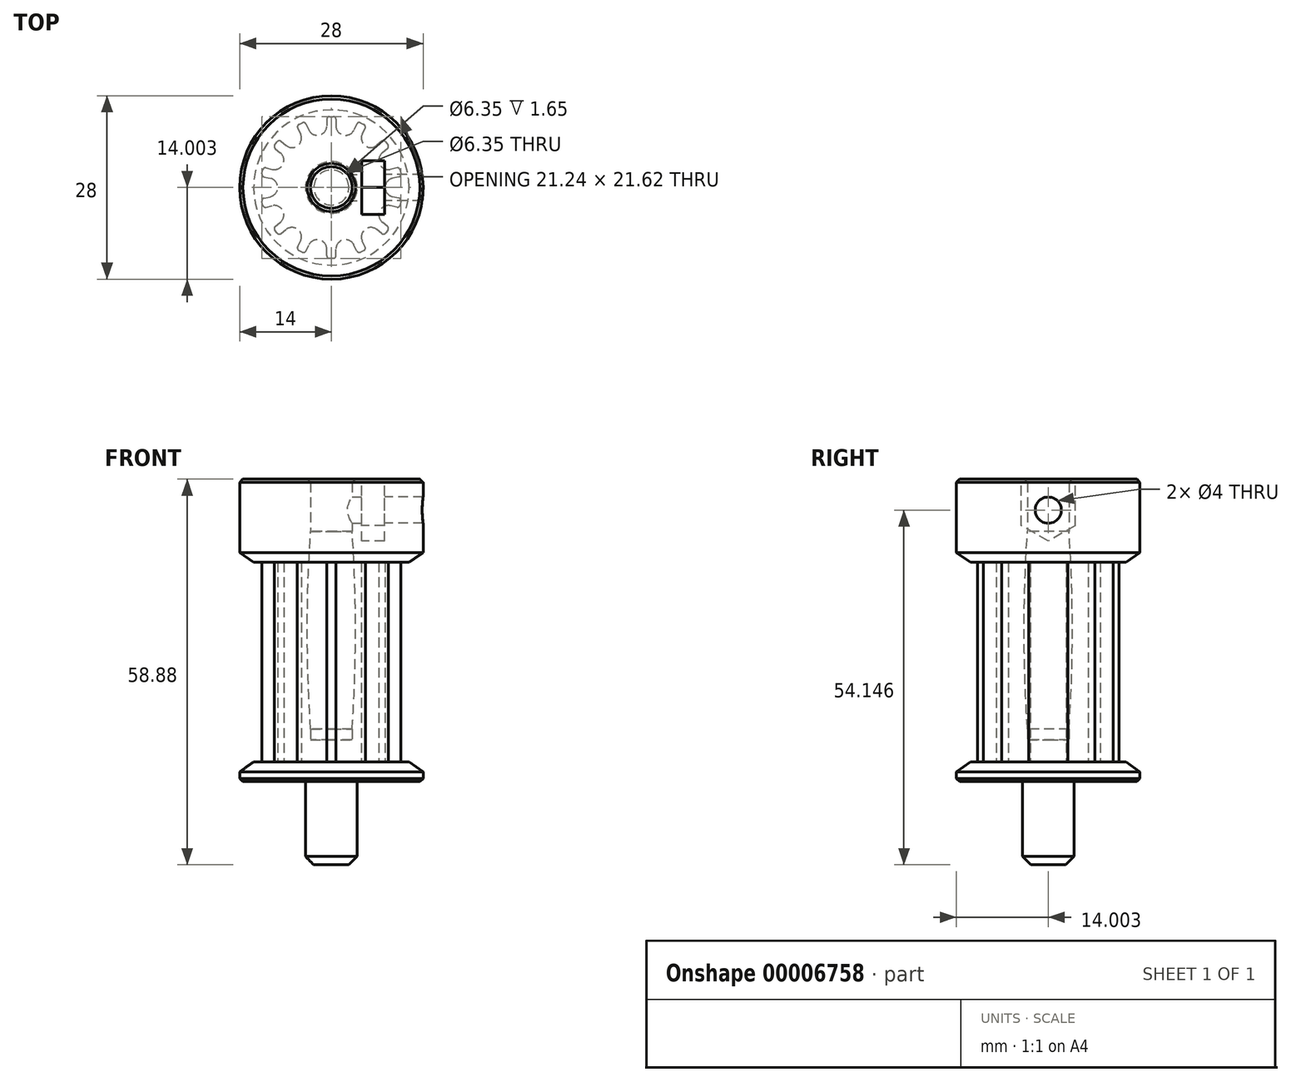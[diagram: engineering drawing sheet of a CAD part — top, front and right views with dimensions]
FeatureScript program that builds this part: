
annotation { "Feature Type Name" : "Feature", "Feature Type Description" : "" }
export const myFeature = defineFeature(function(context is Context, id is Id, definition is map)
    precondition{}
    {
        {
            var Q0;
            Q0=qCreatedBy(makeId("Top.planeOp"),FACE);
            var sketch = newSketch(context, id + "F0", { "sketchPlane" : qUnion([Q0])});
            skLineSegment(sketch, "E0", {"start": v(-0.3, 10.12) * mm, "end": v(0.3, 10.12) * mm});
            skPoint(sketch, "E1", {"position": v(0, 10.12) * mm});
            skArc(sketch, "E2", {"start": v(0.3, 10.12) * mm, "mid": v(0.58, 10) * mm, "end": v(0.7, 9.72) * mm});
            skArc(sketch, "E3", {"start": v(-0.3, 10.12) * mm, "mid": v(-0.58, 10) * mm, "end": v(-0.7, 9.72) * mm});
            skLineSegment(sketch, "E4", {"start": v(-0.7, 9.72) * mm, "end": v(-0.7, 8.72) * mm});
            skLineSegment(sketch, "E5", {"start": v(0.7, 9.72) * mm, "end": v(0.7, 8.72) * mm});
            skArc(sketch, "E6", {"start": v(-0.7, 8.72) * mm, "mid": v(-1.83, 7.3) * mm, "end": v(-3.45, 8.09) * mm});
            skArc(sketch, "E7.1.0", {"start": v(-4.71, 7.48) * mm, "mid": v(-5.12, 5.72) * mm, "end": v(-6.92, 5.72) * mm});
            skLineSegment(sketch, "E7.1.1", {"start": v(-5.15, 8.38) * mm, "end": v(-4.71, 7.48) * mm});
            skArc(sketch, "E7.1.2", {"start": v(-4.96, 8.91) * mm, "mid": v(-5.17, 8.69) * mm, "end": v(-5.15, 8.38) * mm});
            skLineSegment(sketch, "E7.1.3", {"start": v(-4.96, 8.91) * mm, "end": v(-4.42, 9.17) * mm});
            skArc(sketch, "E7.1.4", {"start": v(-4.42, 9.17) * mm, "mid": v(-4.12, 9.2) * mm, "end": v(-3.89, 8.99) * mm});
            skLineSegment(sketch, "E7.1.5", {"start": v(-3.89, 8.99) * mm, "end": v(-3.45, 8.09) * mm});
            skArc(sketch, "E7.2.0", {"start": v(-7.8, 4.62) * mm, "mid": v(-7.4, 2.86) * mm, "end": v(-9.02, 2.08) * mm});
            skLineSegment(sketch, "E7.2.1", {"start": v(-8.58, 5.25) * mm, "end": v(-7.8, 4.62) * mm});
            skArc(sketch, "E7.2.2", {"start": v(-8.64, 5.8) * mm, "mid": v(-8.73, 5.52) * mm, "end": v(-8.58, 5.25) * mm});
            skLineSegment(sketch, "E7.2.3", {"start": v(-8.64, 5.8) * mm, "end": v(-8.27, 6.28) * mm});
            skArc(sketch, "E7.2.4", {"start": v(-8.27, 6.28) * mm, "mid": v(-8, 6.43) * mm, "end": v(-7.7, 6.34) * mm});
            skLineSegment(sketch, "E7.2.5", {"start": v(-7.7, 6.34) * mm, "end": v(-6.92, 5.72) * mm});
            skPoint(sketch, "E7.center", {"position": v(0, -0.7) * mm});
            skArc(sketch, "E8.3.3.0", {"start": v(-9.33, 0.72) * mm, "mid": v(-8.2, -0.7) * mm, "end": v(-9.33, -2.1) * mm});
            skLineSegment(sketch, "E8.4.3.0", {"start": v(-10.3, 0.94) * mm, "end": v(-9.33, 0.72) * mm});
            skArc(sketch, "E8.7.3.0", {"start": v(-10.6, 1.42) * mm, "mid": v(-10.56, 1.11) * mm, "end": v(-10.3, 0.94) * mm});
            skLineSegment(sketch, "E8.11.3.0", {"start": v(-10.6, 1.42) * mm, "end": v(-10.47, 2) * mm});
            skArc(sketch, "E8.14.3.0", {"start": v(-10.47, 2) * mm, "mid": v(-10.3, 2.25) * mm, "end": v(-10, 2.3) * mm});
            skLineSegment(sketch, "E8.18.3.0", {"start": v(-10, 2.3) * mm, "end": v(-9.02, 2.08) * mm});
            skArc(sketch, "E8.3.4.0", {"start": v(-9.02, -3.47) * mm, "mid": v(-7.4, -4.26) * mm, "end": v(-7.8, -6.02) * mm});
            skLineSegment(sketch, "E8.4.4.0", {"start": v(-10, -3.7) * mm, "end": v(-9.02, -3.47) * mm});
            skArc(sketch, "E8.7.4.0", {"start": v(-10.47, -3.4) * mm, "mid": v(-10.3, -3.64) * mm, "end": v(-10, -3.7) * mm});
            skLineSegment(sketch, "E8.11.4.0", {"start": v(-10.47, -3.4) * mm, "end": v(-10.6, -2.81) * mm});
            skArc(sketch, "E8.14.4.0", {"start": v(-10.6, -2.81) * mm, "mid": v(-10.56, -2.5) * mm, "end": v(-10.3, -2.33) * mm});
            skLineSegment(sketch, "E8.18.4.0", {"start": v(-10.3, -2.33) * mm, "end": v(-9.33, -2.1) * mm});
            skArc(sketch, "E8.3.5.0", {"start": v(-6.92, -7.11) * mm, "mid": v(-5.12, -7.11) * mm, "end": v(-4.71, -8.87) * mm});
            skLineSegment(sketch, "E8.4.5.0", {"start": v(-7.7, -7.74) * mm, "end": v(-6.92, -7.11) * mm});
            skArc(sketch, "E8.7.5.0", {"start": v(-8.27, -7.67) * mm, "mid": v(-8, -7.82) * mm, "end": v(-7.7, -7.74) * mm});
            skLineSegment(sketch, "E8.11.5.0", {"start": v(-8.27, -7.67) * mm, "end": v(-8.64, -7.2) * mm});
            skArc(sketch, "E8.14.5.0", {"start": v(-8.64, -7.2) * mm, "mid": v(-8.73, -6.9) * mm, "end": v(-8.58, -6.64) * mm});
            skLineSegment(sketch, "E8.18.5.0", {"start": v(-8.58, -6.64) * mm, "end": v(-7.8, -6.02) * mm});
            skArc(sketch, "E8.3.6.0", {"start": v(-3.45, -9.48) * mm, "mid": v(-1.83, -8.7) * mm, "end": v(-0.7, -10.1) * mm});
            skLineSegment(sketch, "E8.4.6.0", {"start": v(-3.89, -10.38) * mm, "end": v(-3.45, -9.48) * mm});
            skArc(sketch, "E8.7.6.0", {"start": v(-4.42, -10.57) * mm, "mid": v(-4.12, -10.59) * mm, "end": v(-3.89, -10.38) * mm});
            skLineSegment(sketch, "E8.11.6.0", {"start": v(-4.42, -10.57) * mm, "end": v(-4.96, -10.3) * mm});
            skArc(sketch, "E8.14.6.0", {"start": v(-4.96, -10.3) * mm, "mid": v(-5.17, -10.08) * mm, "end": v(-5.15, -9.77) * mm});
            skLineSegment(sketch, "E8.18.6.0", {"start": v(-5.15, -9.77) * mm, "end": v(-4.71, -8.87) * mm});
            skArc(sketch, "E8.3.7.0", {"start": v(0.7, -10.1) * mm, "mid": v(1.83, -8.7) * mm, "end": v(3.45, -9.48) * mm});
            skLineSegment(sketch, "E8.4.7.0", {"start": v(0.7, -11.1) * mm, "end": v(0.7, -10.1) * mm});
            skArc(sketch, "E8.7.7.0", {"start": v(0.3, -11.5) * mm, "mid": v(0.58, -11.4) * mm, "end": v(0.7, -11.1) * mm});
            skLineSegment(sketch, "E8.11.7.0", {"start": v(0.3, -11.5) * mm, "end": v(-0.3, -11.5) * mm});
            skArc(sketch, "E8.14.7.0", {"start": v(-0.3, -11.5) * mm, "mid": v(-0.58, -11.4) * mm, "end": v(-0.7, -11.1) * mm});
            skLineSegment(sketch, "E8.18.7.0", {"start": v(-0.7, -11.1) * mm, "end": v(-0.7, -10.1) * mm});
            skArc(sketch, "E8.3.8.0", {"start": v(4.71, -8.87) * mm, "mid": v(5.12, -7.11) * mm, "end": v(6.92, -7.11) * mm});
            skLineSegment(sketch, "E8.4.8.0", {"start": v(5.15, -9.77) * mm, "end": v(4.71, -8.87) * mm});
            skArc(sketch, "E8.7.8.0", {"start": v(4.96, -10.3) * mm, "mid": v(5.17, -10.08) * mm, "end": v(5.15, -9.77) * mm});
            skLineSegment(sketch, "E8.11.8.0", {"start": v(4.96, -10.3) * mm, "end": v(4.42, -10.57) * mm});
            skArc(sketch, "E8.14.8.0", {"start": v(4.42, -10.57) * mm, "mid": v(4.12, -10.59) * mm, "end": v(3.89, -10.38) * mm});
            skLineSegment(sketch, "E8.18.8.0", {"start": v(3.89, -10.38) * mm, "end": v(3.45, -9.48) * mm});
            skArc(sketch, "E8.3.9.0", {"start": v(7.8, -6.02) * mm, "mid": v(7.4, -4.26) * mm, "end": v(9.02, -3.47) * mm});
            skLineSegment(sketch, "E8.4.9.0", {"start": v(8.58, -6.64) * mm, "end": v(7.8, -6.02) * mm});
            skArc(sketch, "E8.7.9.0", {"start": v(8.64, -7.2) * mm, "mid": v(8.73, -6.9) * mm, "end": v(8.58, -6.64) * mm});
            skLineSegment(sketch, "E8.11.9.0", {"start": v(8.64, -7.2) * mm, "end": v(8.27, -7.67) * mm});
            skArc(sketch, "E8.14.9.0", {"start": v(8.27, -7.67) * mm, "mid": v(8, -7.82) * mm, "end": v(7.7, -7.74) * mm});
            skLineSegment(sketch, "E8.18.9.0", {"start": v(7.7, -7.74) * mm, "end": v(6.92, -7.11) * mm});
            skArc(sketch, "E8.3.10.0", {"start": v(9.33, -2.1) * mm, "mid": v(8.2, -0.7) * mm, "end": v(9.33, 0.72) * mm});
            skLineSegment(sketch, "E8.4.10.0", {"start": v(10.3, -2.33) * mm, "end": v(9.33, -2.1) * mm});
            skArc(sketch, "E8.7.10.0", {"start": v(10.6, -2.81) * mm, "mid": v(10.56, -2.5) * mm, "end": v(10.3, -2.33) * mm});
            skLineSegment(sketch, "E8.11.10.0", {"start": v(10.6, -2.81) * mm, "end": v(10.47, -3.4) * mm});
            skArc(sketch, "E8.14.10.0", {"start": v(10.47, -3.4) * mm, "mid": v(10.3, -3.64) * mm, "end": v(10, -3.7) * mm});
            skLineSegment(sketch, "E8.18.10.0", {"start": v(10, -3.7) * mm, "end": v(9.02, -3.47) * mm});
            skArc(sketch, "E8.3.11.0", {"start": v(9.02, 2.08) * mm, "mid": v(7.4, 2.86) * mm, "end": v(7.8, 4.62) * mm});
            skLineSegment(sketch, "E8.4.11.0", {"start": v(10, 2.3) * mm, "end": v(9.02, 2.08) * mm});
            skArc(sketch, "E8.7.11.0", {"start": v(10.47, 2) * mm, "mid": v(10.3, 2.25) * mm, "end": v(10, 2.3) * mm});
            skLineSegment(sketch, "E8.11.11.0", {"start": v(10.47, 2) * mm, "end": v(10.6, 1.42) * mm});
            skArc(sketch, "E8.14.11.0", {"start": v(10.6, 1.42) * mm, "mid": v(10.56, 1.11) * mm, "end": v(10.3, 0.94) * mm});
            skLineSegment(sketch, "E8.18.11.0", {"start": v(10.3, 0.94) * mm, "end": v(9.33, 0.72) * mm});
            skArc(sketch, "E8.3.12.0", {"start": v(6.92, 5.72) * mm, "mid": v(5.12, 5.72) * mm, "end": v(4.71, 7.48) * mm});
            skLineSegment(sketch, "E8.4.12.0", {"start": v(7.7, 6.34) * mm, "end": v(6.92, 5.72) * mm});
            skArc(sketch, "E8.7.12.0", {"start": v(8.27, 6.28) * mm, "mid": v(8, 6.43) * mm, "end": v(7.7, 6.34) * mm});
            skLineSegment(sketch, "E8.11.12.0", {"start": v(8.27, 6.28) * mm, "end": v(8.64, 5.8) * mm});
            skArc(sketch, "E8.14.12.0", {"start": v(8.64, 5.8) * mm, "mid": v(8.73, 5.52) * mm, "end": v(8.58, 5.25) * mm});
            skLineSegment(sketch, "E8.18.12.0", {"start": v(8.58, 5.25) * mm, "end": v(7.8, 4.62) * mm});
            skArc(sketch, "E8.3.13.0", {"start": v(3.45, 8.09) * mm, "mid": v(1.83, 7.3) * mm, "end": v(0.7, 8.72) * mm});
            skLineSegment(sketch, "E8.4.13.0", {"start": v(3.89, 8.99) * mm, "end": v(3.45, 8.09) * mm});
            skArc(sketch, "E8.7.13.0", {"start": v(4.42, 9.17) * mm, "mid": v(4.12, 9.2) * mm, "end": v(3.89, 8.99) * mm});
            skLineSegment(sketch, "E8.11.13.0", {"start": v(4.42, 9.17) * mm, "end": v(4.96, 8.91) * mm});
            skArc(sketch, "E8.14.13.0", {"start": v(4.96, 8.91) * mm, "mid": v(5.17, 8.69) * mm, "end": v(5.15, 8.38) * mm});
            skLineSegment(sketch, "E8.18.13.0", {"start": v(5.15, 8.38) * mm, "end": v(4.71, 7.48) * mm});
            skCircle(sketch, "E9", {"center": v(0, -0.7) * mm, "radius": 10.81 * mm, "construction": true});
            skCircle(sketch, "E10", {"center": v(0, -0.7) * mm, "radius": 3.18 * mm});
            skSolve(sketch);
        }
        {
            var Q0;
            Q0=makeQuery(id+"F0.imprint","IMPRINT",FACE,{"disambiguationData":[TD([[makeQuery(id+"F0.imprint","IMPRINT",EDGE,{"derivedFrom":sQuery(id+"F0.wireOp",EDGE,"E0")}),-1.0]])]});
            extrude(context, id + "F1", {"entities" : qUnion([Q0]), "endBound" : BoundingType.SYMMETRIC, "depth" : 30.48 * mm, "offsetDistance" : 25 * mm});
        }
        {
            var Q0;
            Q0=makeQuery(id+"F1.opExtrude","CAP_FACE",FACE,{"disambiguationData":[OSD([sQuery(id+"F0.wireOp",EDGE,"E0"),sQuery(id+"F0.wireOp",EDGE,"E2"),sQuery(id+"F0.wireOp",EDGE,"E3"),sQuery(id+"F0.wireOp",EDGE,"E4"),sQuery(id+"F0.wireOp",EDGE,"E5"),sQuery(id+"F0.wireOp",EDGE,"E6"),sQuery(id+"F0.wireOp",EDGE,"E7.1.0"),sQuery(id+"F0.wireOp",EDGE,"E7.1.1"),sQuery(id+"F0.wireOp",EDGE,"E7.1.2"),sQuery(id+"F0.wireOp",EDGE,"E7.1.3"),sQuery(id+"F0.wireOp",EDGE,"E7.1.4"),sQuery(id+"F0.wireOp",EDGE,"E7.1.5"),sQuery(id+"F0.wireOp",EDGE,"E7.2.0"),sQuery(id+"F0.wireOp",EDGE,"E7.2.1"),sQuery(id+"F0.wireOp",EDGE,"E7.2.2"),sQuery(id+"F0.wireOp",EDGE,"E7.2.3"),sQuery(id+"F0.wireOp",EDGE,"E7.2.4"),sQuery(id+"F0.wireOp",EDGE,"E7.2.5"),sQuery(id+"F0.wireOp",EDGE,"E8.3.3.0"),sQuery(id+"F0.wireOp",EDGE,"E8.4.3.0"),sQuery(id+"F0.wireOp",EDGE,"E8.7.3.0"),sQuery(id+"F0.wireOp",EDGE,"E8.11.3.0"),sQuery(id+"F0.wireOp",EDGE,"E8.14.3.0"),sQuery(id+"F0.wireOp",EDGE,"E8.18.3.0"),sQuery(id+"F0.wireOp",EDGE,"E8.3.4.0"),sQuery(id+"F0.wireOp",EDGE,"E8.4.4.0"),sQuery(id+"F0.wireOp",EDGE,"E8.7.4.0"),sQuery(id+"F0.wireOp",EDGE,"E8.11.4.0"),sQuery(id+"F0.wireOp",EDGE,"E8.14.4.0"),sQuery(id+"F0.wireOp",EDGE,"E8.18.4.0"),sQuery(id+"F0.wireOp",EDGE,"E8.3.5.0"),sQuery(id+"F0.wireOp",EDGE,"E8.4.5.0"),sQuery(id+"F0.wireOp",EDGE,"E8.7.5.0"),sQuery(id+"F0.wireOp",EDGE,"E8.11.5.0"),sQuery(id+"F0.wireOp",EDGE,"E8.14.5.0"),sQuery(id+"F0.wireOp",EDGE,"E8.18.5.0"),sQuery(id+"F0.wireOp",EDGE,"E8.3.6.0"),sQuery(id+"F0.wireOp",EDGE,"E8.4.6.0"),sQuery(id+"F0.wireOp",EDGE,"E8.7.6.0"),sQuery(id+"F0.wireOp",EDGE,"E8.11.6.0"),sQuery(id+"F0.wireOp",EDGE,"E8.14.6.0"),sQuery(id+"F0.wireOp",EDGE,"E8.18.6.0"),sQuery(id+"F0.wireOp",EDGE,"E8.3.7.0"),sQuery(id+"F0.wireOp",EDGE,"E8.4.7.0"),sQuery(id+"F0.wireOp",EDGE,"E8.7.7.0"),sQuery(id+"F0.wireOp",EDGE,"E8.11.7.0"),sQuery(id+"F0.wireOp",EDGE,"E8.14.7.0"),sQuery(id+"F0.wireOp",EDGE,"E8.18.7.0"),sQuery(id+"F0.wireOp",EDGE,"E8.3.8.0"),sQuery(id+"F0.wireOp",EDGE,"E8.4.8.0"),sQuery(id+"F0.wireOp",EDGE,"E8.7.8.0"),sQuery(id+"F0.wireOp",EDGE,"E8.11.8.0"),sQuery(id+"F0.wireOp",EDGE,"E8.14.8.0"),sQuery(id+"F0.wireOp",EDGE,"E8.18.8.0"),sQuery(id+"F0.wireOp",EDGE,"E8.3.9.0"),sQuery(id+"F0.wireOp",EDGE,"E8.4.9.0"),sQuery(id+"F0.wireOp",EDGE,"E8.7.9.0"),sQuery(id+"F0.wireOp",EDGE,"E8.11.9.0"),sQuery(id+"F0.wireOp",EDGE,"E8.14.9.0"),sQuery(id+"F0.wireOp",EDGE,"E8.18.9.0"),sQuery(id+"F0.wireOp",EDGE,"E8.3.10.0"),sQuery(id+"F0.wireOp",EDGE,"E8.4.10.0"),sQuery(id+"F0.wireOp",EDGE,"E8.7.10.0"),sQuery(id+"F0.wireOp",EDGE,"E8.11.10.0"),sQuery(id+"F0.wireOp",EDGE,"E8.14.10.0"),sQuery(id+"F0.wireOp",EDGE,"E8.18.10.0"),sQuery(id+"F0.wireOp",EDGE,"E8.3.11.0"),sQuery(id+"F0.wireOp",EDGE,"E8.4.11.0"),sQuery(id+"F0.wireOp",EDGE,"E8.7.11.0"),sQuery(id+"F0.wireOp",EDGE,"E8.11.11.0"),sQuery(id+"F0.wireOp",EDGE,"E8.14.11.0"),sQuery(id+"F0.wireOp",EDGE,"E8.18.11.0"),sQuery(id+"F0.wireOp",EDGE,"E8.3.12.0"),sQuery(id+"F0.wireOp",EDGE,"E8.4.12.0"),sQuery(id+"F0.wireOp",EDGE,"E8.7.12.0"),sQuery(id+"F0.wireOp",EDGE,"E8.11.12.0"),sQuery(id+"F0.wireOp",EDGE,"E8.14.12.0"),sQuery(id+"F0.wireOp",EDGE,"E8.18.12.0"),sQuery(id+"F0.wireOp",EDGE,"E8.3.13.0"),sQuery(id+"F0.wireOp",EDGE,"E8.4.13.0"),sQuery(id+"F0.wireOp",EDGE,"E8.7.13.0"),sQuery(id+"F0.wireOp",EDGE,"E8.11.13.0"),sQuery(id+"F0.wireOp",EDGE,"E8.14.13.0"),sQuery(id+"F0.wireOp",EDGE,"E8.18.13.0"),sQuery(id+"F0.wireOp",EDGE,"c70ca20e-aa8e-449a-a5f3-8252f9445d40.3.14.0"),sQuery(id+"F0.wireOp",EDGE,"c70ca20e-aa8e-449a-a5f3-8252f9445d40.4.14.0"),sQuery(id+"F0.wireOp",EDGE,"c70ca20e-aa8e-449a-a5f3-8252f9445d40.7.14.0"),sQuery(id+"F0.wireOp",EDGE,"c70ca20e-aa8e-449a-a5f3-8252f9445d40.11.14.0"),sQuery(id+"F0.wireOp",EDGE,"c70ca20e-aa8e-449a-a5f3-8252f9445d40.14.14.0"),sQuery(id+"F0.wireOp",EDGE,"c70ca20e-aa8e-449a-a5f3-8252f9445d40.18.14.0"),sQuery(id+"F0.wireOp",EDGE,"c70ca20e-aa8e-449a-a5f3-8252f9445d40.3.15.0"),sQuery(id+"F0.wireOp",EDGE,"c70ca20e-aa8e-449a-a5f3-8252f9445d40.4.15.0"),sQuery(id+"F0.wireOp",EDGE,"c70ca20e-aa8e-449a-a5f3-8252f9445d40.7.15.0"),sQuery(id+"F0.wireOp",EDGE,"c70ca20e-aa8e-449a-a5f3-8252f9445d40.11.15.0"),sQuery(id+"F0.wireOp",EDGE,"c70ca20e-aa8e-449a-a5f3-8252f9445d40.14.15.0"),sQuery(id+"F0.wireOp",EDGE,"c70ca20e-aa8e-449a-a5f3-8252f9445d40.18.15.0"),sQuery(id+"F0.wireOp",EDGE,"c70ca20e-aa8e-449a-a5f3-8252f9445d40.3.16.0"),sQuery(id+"F0.wireOp",EDGE,"c70ca20e-aa8e-449a-a5f3-8252f9445d40.4.16.0"),sQuery(id+"F0.wireOp",EDGE,"c70ca20e-aa8e-449a-a5f3-8252f9445d40.7.16.0"),sQuery(id+"F0.wireOp",EDGE,"c70ca20e-aa8e-449a-a5f3-8252f9445d40.11.16.0"),sQuery(id+"F0.wireOp",EDGE,"c70ca20e-aa8e-449a-a5f3-8252f9445d40.14.16.0"),sQuery(id+"F0.wireOp",EDGE,"c70ca20e-aa8e-449a-a5f3-8252f9445d40.18.16.0"),sQuery(id+"F0.wireOp",EDGE,"c70ca20e-aa8e-449a-a5f3-8252f9445d40.3.17.0"),sQuery(id+"F0.wireOp",EDGE,"c70ca20e-aa8e-449a-a5f3-8252f9445d40.4.17.0"),sQuery(id+"F0.wireOp",EDGE,"c70ca20e-aa8e-449a-a5f3-8252f9445d40.7.17.0"),sQuery(id+"F0.wireOp",EDGE,"c70ca20e-aa8e-449a-a5f3-8252f9445d40.11.17.0"),sQuery(id+"F0.wireOp",EDGE,"c70ca20e-aa8e-449a-a5f3-8252f9445d40.14.17.0"),sQuery(id+"F0.wireOp",EDGE,"c70ca20e-aa8e-449a-a5f3-8252f9445d40.18.17.0"),sQuery(id+"F0.wireOp",EDGE,"c70ca20e-aa8e-449a-a5f3-8252f9445d40.3.18.0"),sQuery(id+"F0.wireOp",EDGE,"c70ca20e-aa8e-449a-a5f3-8252f9445d40.4.18.0"),sQuery(id+"F0.wireOp",EDGE,"c70ca20e-aa8e-449a-a5f3-8252f9445d40.7.18.0"),sQuery(id+"F0.wireOp",EDGE,"c70ca20e-aa8e-449a-a5f3-8252f9445d40.11.18.0"),sQuery(id+"F0.wireOp",EDGE,"c70ca20e-aa8e-449a-a5f3-8252f9445d40.14.18.0"),sQuery(id+"F0.wireOp",EDGE,"c70ca20e-aa8e-449a-a5f3-8252f9445d40.18.18.0"),sQuery(id+"F0.wireOp",EDGE,"c70ca20e-aa8e-449a-a5f3-8252f9445d40.3.19.0"),sQuery(id+"F0.wireOp",EDGE,"c70ca20e-aa8e-449a-a5f3-8252f9445d40.4.19.0"),sQuery(id+"F0.wireOp",EDGE,"c70ca20e-aa8e-449a-a5f3-8252f9445d40.7.19.0"),sQuery(id+"F0.wireOp",EDGE,"c70ca20e-aa8e-449a-a5f3-8252f9445d40.11.19.0"),sQuery(id+"F0.wireOp",EDGE,"c70ca20e-aa8e-449a-a5f3-8252f9445d40.14.19.0"),sQuery(id+"F0.wireOp",EDGE,"c70ca20e-aa8e-449a-a5f3-8252f9445d40.18.19.0")])],"isStart":false});
            var sketch = newSketch(context, id + "F2", { "sketchPlane" : qUnion([Q0])});
            skCircle(sketch, "E11", {"center": v(0, -0.7) * mm, "radius": 14 * mm});
            skSolve(sketch);
        }
        {
            var Q0;
            Q0=makeQuery(id+"F2.imprint","IMPRINT",FACE,{"disambiguationData":[TD([[makeQuery(id+"F2.imprint","IMPRINT",EDGE,{"derivedFrom":makeQuery(id+"F1.opExtrude","CAP_EDGE",EDGE,{"disambiguationData":[OSD([sQuery(id+"F0.wireOp",EDGE,"E0")])],"isStart":false})}),-1.0]])]});
            var Q1;
            Q1=makeQuery(id+"F2.imprint","IMPRINT",FACE,{"disambiguationData":[TD([[makeQuery(id+"F2.imprint","IMPRINT",EDGE,{"derivedFrom":sQuery(id+"F2.wireOp",EDGE,"E11")}),1.0]])]});
            extrude(context, id + "F3", {"entities" : qUnion([Q0, Q1]), "operationType" : NewBodyOperationType.ADD, "depth" : 12.7 * mm, "offsetDistance" : 25 * mm});
        }
        {
            var Q0;
            Q0=makeQuery(id+"F1.opExtrude","CAP_FACE",FACE,{"disambiguationData":[OSD([sQuery(id+"F0.wireOp",EDGE,"E0"),sQuery(id+"F0.wireOp",EDGE,"E2"),sQuery(id+"F0.wireOp",EDGE,"E3"),sQuery(id+"F0.wireOp",EDGE,"E4"),sQuery(id+"F0.wireOp",EDGE,"E5"),sQuery(id+"F0.wireOp",EDGE,"E6"),sQuery(id+"F0.wireOp",EDGE,"E7.1.0"),sQuery(id+"F0.wireOp",EDGE,"E7.1.1"),sQuery(id+"F0.wireOp",EDGE,"E7.1.2"),sQuery(id+"F0.wireOp",EDGE,"E7.1.3"),sQuery(id+"F0.wireOp",EDGE,"E7.1.4"),sQuery(id+"F0.wireOp",EDGE,"E7.1.5"),sQuery(id+"F0.wireOp",EDGE,"E7.2.0"),sQuery(id+"F0.wireOp",EDGE,"E7.2.1"),sQuery(id+"F0.wireOp",EDGE,"E7.2.2"),sQuery(id+"F0.wireOp",EDGE,"E7.2.3"),sQuery(id+"F0.wireOp",EDGE,"E7.2.4"),sQuery(id+"F0.wireOp",EDGE,"E7.2.5"),sQuery(id+"F0.wireOp",EDGE,"E8.3.3.0"),sQuery(id+"F0.wireOp",EDGE,"E8.4.3.0"),sQuery(id+"F0.wireOp",EDGE,"E8.7.3.0"),sQuery(id+"F0.wireOp",EDGE,"E8.11.3.0"),sQuery(id+"F0.wireOp",EDGE,"E8.14.3.0"),sQuery(id+"F0.wireOp",EDGE,"E8.18.3.0"),sQuery(id+"F0.wireOp",EDGE,"E8.3.4.0"),sQuery(id+"F0.wireOp",EDGE,"E8.4.4.0"),sQuery(id+"F0.wireOp",EDGE,"E8.7.4.0"),sQuery(id+"F0.wireOp",EDGE,"E8.11.4.0"),sQuery(id+"F0.wireOp",EDGE,"E8.14.4.0"),sQuery(id+"F0.wireOp",EDGE,"E8.18.4.0"),sQuery(id+"F0.wireOp",EDGE,"E8.3.5.0"),sQuery(id+"F0.wireOp",EDGE,"E8.4.5.0"),sQuery(id+"F0.wireOp",EDGE,"E8.7.5.0"),sQuery(id+"F0.wireOp",EDGE,"E8.11.5.0"),sQuery(id+"F0.wireOp",EDGE,"E8.14.5.0"),sQuery(id+"F0.wireOp",EDGE,"E8.18.5.0"),sQuery(id+"F0.wireOp",EDGE,"E8.3.6.0"),sQuery(id+"F0.wireOp",EDGE,"E8.4.6.0"),sQuery(id+"F0.wireOp",EDGE,"E8.7.6.0"),sQuery(id+"F0.wireOp",EDGE,"E8.11.6.0"),sQuery(id+"F0.wireOp",EDGE,"E8.14.6.0"),sQuery(id+"F0.wireOp",EDGE,"E8.18.6.0"),sQuery(id+"F0.wireOp",EDGE,"E8.3.7.0"),sQuery(id+"F0.wireOp",EDGE,"E8.4.7.0"),sQuery(id+"F0.wireOp",EDGE,"E8.7.7.0"),sQuery(id+"F0.wireOp",EDGE,"E8.11.7.0"),sQuery(id+"F0.wireOp",EDGE,"E8.14.7.0"),sQuery(id+"F0.wireOp",EDGE,"E8.18.7.0"),sQuery(id+"F0.wireOp",EDGE,"E8.3.8.0"),sQuery(id+"F0.wireOp",EDGE,"E8.4.8.0"),sQuery(id+"F0.wireOp",EDGE,"E8.7.8.0"),sQuery(id+"F0.wireOp",EDGE,"E8.11.8.0"),sQuery(id+"F0.wireOp",EDGE,"E8.14.8.0"),sQuery(id+"F0.wireOp",EDGE,"E8.18.8.0"),sQuery(id+"F0.wireOp",EDGE,"E8.3.9.0"),sQuery(id+"F0.wireOp",EDGE,"E8.4.9.0"),sQuery(id+"F0.wireOp",EDGE,"E8.7.9.0"),sQuery(id+"F0.wireOp",EDGE,"E8.11.9.0"),sQuery(id+"F0.wireOp",EDGE,"E8.14.9.0"),sQuery(id+"F0.wireOp",EDGE,"E8.18.9.0"),sQuery(id+"F0.wireOp",EDGE,"E8.3.10.0"),sQuery(id+"F0.wireOp",EDGE,"E8.4.10.0"),sQuery(id+"F0.wireOp",EDGE,"E8.7.10.0"),sQuery(id+"F0.wireOp",EDGE,"E8.11.10.0"),sQuery(id+"F0.wireOp",EDGE,"E8.14.10.0"),sQuery(id+"F0.wireOp",EDGE,"E8.18.10.0"),sQuery(id+"F0.wireOp",EDGE,"E8.3.11.0"),sQuery(id+"F0.wireOp",EDGE,"E8.4.11.0"),sQuery(id+"F0.wireOp",EDGE,"E8.7.11.0"),sQuery(id+"F0.wireOp",EDGE,"E8.11.11.0"),sQuery(id+"F0.wireOp",EDGE,"E8.14.11.0"),sQuery(id+"F0.wireOp",EDGE,"E8.18.11.0"),sQuery(id+"F0.wireOp",EDGE,"E8.3.12.0"),sQuery(id+"F0.wireOp",EDGE,"E8.4.12.0"),sQuery(id+"F0.wireOp",EDGE,"E8.7.12.0"),sQuery(id+"F0.wireOp",EDGE,"E8.11.12.0"),sQuery(id+"F0.wireOp",EDGE,"E8.14.12.0"),sQuery(id+"F0.wireOp",EDGE,"E8.18.12.0"),sQuery(id+"F0.wireOp",EDGE,"E8.3.13.0"),sQuery(id+"F0.wireOp",EDGE,"E8.4.13.0"),sQuery(id+"F0.wireOp",EDGE,"E8.7.13.0"),sQuery(id+"F0.wireOp",EDGE,"E8.11.13.0"),sQuery(id+"F0.wireOp",EDGE,"E8.14.13.0"),sQuery(id+"F0.wireOp",EDGE,"E8.18.13.0"),sQuery(id+"F0.wireOp",EDGE,"c70ca20e-aa8e-449a-a5f3-8252f9445d40.3.14.0"),sQuery(id+"F0.wireOp",EDGE,"c70ca20e-aa8e-449a-a5f3-8252f9445d40.4.14.0"),sQuery(id+"F0.wireOp",EDGE,"c70ca20e-aa8e-449a-a5f3-8252f9445d40.7.14.0"),sQuery(id+"F0.wireOp",EDGE,"c70ca20e-aa8e-449a-a5f3-8252f9445d40.11.14.0"),sQuery(id+"F0.wireOp",EDGE,"c70ca20e-aa8e-449a-a5f3-8252f9445d40.14.14.0"),sQuery(id+"F0.wireOp",EDGE,"c70ca20e-aa8e-449a-a5f3-8252f9445d40.18.14.0"),sQuery(id+"F0.wireOp",EDGE,"c70ca20e-aa8e-449a-a5f3-8252f9445d40.3.15.0"),sQuery(id+"F0.wireOp",EDGE,"c70ca20e-aa8e-449a-a5f3-8252f9445d40.4.15.0"),sQuery(id+"F0.wireOp",EDGE,"c70ca20e-aa8e-449a-a5f3-8252f9445d40.7.15.0"),sQuery(id+"F0.wireOp",EDGE,"c70ca20e-aa8e-449a-a5f3-8252f9445d40.11.15.0"),sQuery(id+"F0.wireOp",EDGE,"c70ca20e-aa8e-449a-a5f3-8252f9445d40.14.15.0"),sQuery(id+"F0.wireOp",EDGE,"c70ca20e-aa8e-449a-a5f3-8252f9445d40.18.15.0"),sQuery(id+"F0.wireOp",EDGE,"c70ca20e-aa8e-449a-a5f3-8252f9445d40.3.16.0"),sQuery(id+"F0.wireOp",EDGE,"c70ca20e-aa8e-449a-a5f3-8252f9445d40.4.16.0"),sQuery(id+"F0.wireOp",EDGE,"c70ca20e-aa8e-449a-a5f3-8252f9445d40.7.16.0"),sQuery(id+"F0.wireOp",EDGE,"c70ca20e-aa8e-449a-a5f3-8252f9445d40.11.16.0"),sQuery(id+"F0.wireOp",EDGE,"c70ca20e-aa8e-449a-a5f3-8252f9445d40.14.16.0"),sQuery(id+"F0.wireOp",EDGE,"c70ca20e-aa8e-449a-a5f3-8252f9445d40.18.16.0"),sQuery(id+"F0.wireOp",EDGE,"c70ca20e-aa8e-449a-a5f3-8252f9445d40.3.17.0"),sQuery(id+"F0.wireOp",EDGE,"c70ca20e-aa8e-449a-a5f3-8252f9445d40.4.17.0"),sQuery(id+"F0.wireOp",EDGE,"c70ca20e-aa8e-449a-a5f3-8252f9445d40.7.17.0"),sQuery(id+"F0.wireOp",EDGE,"c70ca20e-aa8e-449a-a5f3-8252f9445d40.11.17.0"),sQuery(id+"F0.wireOp",EDGE,"c70ca20e-aa8e-449a-a5f3-8252f9445d40.14.17.0"),sQuery(id+"F0.wireOp",EDGE,"c70ca20e-aa8e-449a-a5f3-8252f9445d40.18.17.0"),sQuery(id+"F0.wireOp",EDGE,"c70ca20e-aa8e-449a-a5f3-8252f9445d40.3.18.0"),sQuery(id+"F0.wireOp",EDGE,"c70ca20e-aa8e-449a-a5f3-8252f9445d40.4.18.0"),sQuery(id+"F0.wireOp",EDGE,"c70ca20e-aa8e-449a-a5f3-8252f9445d40.7.18.0"),sQuery(id+"F0.wireOp",EDGE,"c70ca20e-aa8e-449a-a5f3-8252f9445d40.11.18.0"),sQuery(id+"F0.wireOp",EDGE,"c70ca20e-aa8e-449a-a5f3-8252f9445d40.14.18.0"),sQuery(id+"F0.wireOp",EDGE,"c70ca20e-aa8e-449a-a5f3-8252f9445d40.18.18.0"),sQuery(id+"F0.wireOp",EDGE,"c70ca20e-aa8e-449a-a5f3-8252f9445d40.3.19.0"),sQuery(id+"F0.wireOp",EDGE,"c70ca20e-aa8e-449a-a5f3-8252f9445d40.4.19.0"),sQuery(id+"F0.wireOp",EDGE,"c70ca20e-aa8e-449a-a5f3-8252f9445d40.7.19.0"),sQuery(id+"F0.wireOp",EDGE,"c70ca20e-aa8e-449a-a5f3-8252f9445d40.11.19.0"),sQuery(id+"F0.wireOp",EDGE,"c70ca20e-aa8e-449a-a5f3-8252f9445d40.14.19.0"),sQuery(id+"F0.wireOp",EDGE,"c70ca20e-aa8e-449a-a5f3-8252f9445d40.18.19.0"),sQuery(id+"F0.wireOp",EDGE,"E10")])],"isStart":true});
            var sketch = newSketch(context, id + "F4", { "sketchPlane" : qUnion([Q0])});
            skCircle(sketch, "E12", {"center": v(0, 0.7) * mm, "radius": 14 * mm});
            skSolve(sketch);
        }
        {
            var Q0;
            Q0=makeQuery(id+"F4.imprint","IMPRINT",FACE,{"disambiguationData":[TD([[makeQuery(id+"F4.imprint","IMPRINT",EDGE,{"derivedFrom":makeQuery(id+"F1.opExtrude","CAP_EDGE",EDGE,{"disambiguationData":[OSD([sQuery(id+"F0.wireOp",EDGE,"E0")])],"isStart":true})}),1.0]])]});
            var Q1;
            Q1=makeQuery(id+"F4.imprint","IMPRINT",FACE,{"disambiguationData":[TD([[makeQuery(id+"F4.imprint","IMPRINT",EDGE,{"derivedFrom":sQuery(id+"F4.wireOp",EDGE,"E12")}),1.0]])]});
            extrude(context, id + "F5", {"entities" : qUnion([Q0, Q1]), "operationType" : NewBodyOperationType.ADD, "depth" : 3 * mm, "offsetDistance" : 25 * mm});
        }
        {
            var Q0;
            Q0=makeQuery(id+"F3.opExtrude","CAP_EDGE",EDGE,{"disambiguationData":[OSD([sQuery(id+"F2.wireOp",EDGE,"E11")])],"isStart":true});
            var Q1;
            Q1=makeQuery(id+"F5.opExtrude","CAP_EDGE",EDGE,{"disambiguationData":[OSD([sQuery(id+"F4.wireOp",EDGE,"E12")])],"isStart":true});
            chamfer(context, id + "F6", {"entities" : qUnion([Q0, Q1]), "chamferType" : ChamferType.OFFSET_ANGLE, "width" : 1.5 * mm, "oppositeDirection" : false, "angle" : 55 * degree, "tangentPropagation" : true});
        }
        {
            var Q0;
            Q0=qCreatedBy(makeId("Right.planeOp"),FACE);
            cPlane(context, id + "F7", {"entities" : qUnion([Q0]), "cplaneType" : CPlaneType.OFFSET, "offset" : 6.35 * mm, "width" : 150 * mm, "height" : 150 * mm});
        }
        {
            var Q0;
            Q0=qCreatedBy(id+"F7.planeOp",FACE);
            var sketch = newSketch(context, id + "F8", { "sketchPlane" : qUnion([Q0])});
            skLineSegment(sketch, "E13.0", {"start": v(-3.87, 27.94) * mm, "end": v(2.48, 27.94) * mm});
            skLineSegment(sketch, "E14", {"start": v(-4.8, 27.94) * mm, "end": v(-4.8, 25.57) * mm});
            skLineSegment(sketch, "E15", {"start": v(3.4, 25.57) * mm, "end": v(3.4, 27.94) * mm});
            skPoint(sketch, "E16", {"position": v(-0.7, 27.94) * mm});
            skCircle(sketch, "E17.cCircle", {"center": v(-0.7, 23.2) * mm, "radius": 4.1 * mm, "construction": true});
            skLineSegment(sketch, "E17.0", {"start": v(-4.8, 20.84) * mm, "end": v(-4.8, 25.57) * mm});
            skLineSegment(sketch, "E17.1", {"start": v(-4.8, 25.57) * mm, "end": v(-0.7, 27.94) * mm});
            skLineSegment(sketch, "E17.2", {"start": v(-0.7, 27.94) * mm, "end": v(3.4, 25.57) * mm});
            skLineSegment(sketch, "E17.3", {"start": v(3.4, 25.57) * mm, "end": v(3.4, 20.84) * mm});
            skLineSegment(sketch, "E17.4", {"start": v(3.4, 20.84) * mm, "end": v(-0.7, 18.47) * mm});
            skLineSegment(sketch, "E17.5", {"start": v(-0.7, 18.47) * mm, "end": v(-4.8, 20.84) * mm});
            skPoint(sketch, "E17.0.midPoint", {"position": v(-4.8, 23.2) * mm});
            skCircle(sketch, "E18", {"center": v(-0.7, 23.2) * mm, "radius": 2 * mm});
            skLineSegment(sketch, "E19", {"start": v(-3.87, 27.94) * mm, "end": v(-4.8, 27.94) * mm});
            skLineSegment(sketch, "E20", {"start": v(2.48, 27.94) * mm, "end": v(3.4, 27.94) * mm});
            skSolve(sketch);
        }
        {
            var Q0;
            {var subQ0=sQuery(id+"F8.wireOp",EDGE,"E15");Q0=makeQuery(id+"F8.imprint","IMPRINT",FACE,{"disambiguationData":[TD([[makeQuery(id+"F8.imprint","IMPRINT",EDGE,{"derivedFrom":subQ0}),1.0]])]});}
            var Q1;
            Q1=makeQuery(id+"F8.imprint","IMPRINT",FACE,{"disambiguationData":[TD([[makeQuery(id+"F8.imprint","IMPRINT",EDGE,{"derivedFrom":sQuery(id+"F8.wireOp",EDGE,"E17.0")}),-1.0]])]});
            var Q2;
            Q2=makeQuery(id+"F8.imprint","IMPRINT",FACE,{"disambiguationData":[TD([[makeQuery(id+"F8.imprint","IMPRINT",EDGE,{"derivedFrom":sQuery(id+"F8.wireOp",EDGE,"E18")}),1.0]])]});
            var Q3;
            {var subQ0=sQuery(id+"F8.wireOp",EDGE,"E14");Q3=makeQuery(id+"F8.imprint","IMPRINT",FACE,{"disambiguationData":[TD([[makeQuery(id+"F8.imprint","IMPRINT",EDGE,{"derivedFrom":subQ0}),1.0]])]});}
            extrude(context, id + "F9", {"entities" : qUnion([Q0, Q1, Q2, Q3]), "operationType" : NewBodyOperationType.REMOVE, "endBound" : BoundingType.SYMMETRIC, "depth" : 3.5 * mm, "offsetDistance" : 25 * mm});
        }
        {
            var Q0;
            Q0=makeQuery(id+"F8.imprint","IMPRINT",FACE,{"disambiguationData":[TD([[makeQuery(id+"F8.imprint","IMPRINT",EDGE,{"derivedFrom":sQuery(id+"F8.wireOp",EDGE,"E18")}),1.0]])]});
            var Q1;
            {var subQ0=sQuery(id+"F0.wireOp",EDGE,"E10");Q1=makeQuery(id+"F3.boolean.opBoolean","MERGE",FACE,{"derivedFrom":[makeQuery(id+"F1.opExtrude","SWEPT_FACE",FACE,{"disambiguationData":[OSD([subQ0])]}),makeQuery(id+"F3.opExtrude","SWEPT_FACE",FACE,{"disambiguationData":[OSD([subQ0])]})]});}
            extrude(context, id + "F10", {"entities" : qUnion([Q0]), "operationType" : NewBodyOperationType.REMOVE, "endBound" : BoundingType.THROUGH_ALL, "depth" : 25 * mm, "endBoundEntityFace" : qUnion([Q1]), "offsetDistance" : 25 * mm});
        }
        {
            var Q0;
            Q0=makeQuery(id+"F8.imprint","IMPRINT",FACE,{"disambiguationData":[TD([[makeQuery(id+"F8.imprint","IMPRINT",EDGE,{"derivedFrom":sQuery(id+"F8.wireOp",EDGE,"E18")}),1.0]])]});
            var Q1;
            {var subQ0=sQuery(id+"F0.wireOp",EDGE,"E10");Q1=makeQuery(id+"F5.boolean.opBoolean","MERGE",FACE,{"derivedFrom":[makeQuery(id+"F3.boolean.opBoolean","MERGE",FACE,{"derivedFrom":[makeQuery(id+"F1.opExtrude","SWEPT_FACE",FACE,{"disambiguationData":[OSD([subQ0])]}),makeQuery(id+"F3.opExtrude","SWEPT_FACE",FACE,{"disambiguationData":[OSD([subQ0])]})]}),makeQuery(id+"F5.opExtrude","SWEPT_FACE",FACE,{"disambiguationData":[OSD([subQ0])]})]});}
            extrude(context, id + "F11", {"entities" : qUnion([Q0]), "operationType" : NewBodyOperationType.REMOVE, "endBound" : BoundingType.UP_TO_SURFACE, "oppositeDirection" : true, "depth" : 25 * mm, "endBoundEntityFace" : qUnion([Q1]), "offsetDistance" : 25 * mm});
        }
        {
            var Q0;
            Q0=makeQuery(id+"F3.opExtrude","CAP_EDGE",EDGE,{"disambiguationData":[OSD([sQuery(id+"F0.wireOp",EDGE,"E10")])],"isStart":false});
            var Q1;
            Q1=makeQuery(id+"F3.opExtrude","CAP_EDGE",EDGE,{"disambiguationData":[OSD([sQuery(id+"F2.wireOp",EDGE,"E11")])],"isStart":false});
            var Q2;
            Q2=makeQuery(id+"F5.opExtrude","CAP_EDGE",EDGE,{"disambiguationData":[OSD([sQuery(id+"F4.wireOp",EDGE,"E12")])],"isStart":false});
            var Q3;
            Q3=makeQuery(id+"F9.boolean.opBoolean","COPY",EDGE,{"derivedFrom":makeQuery(id+"F9.opExtrude","CAP_EDGE",EDGE,{"disambiguationData":[OSD([sQuery(id+"F8.wireOp",EDGE,"E13.0")])],"isStart":true})});
            var Q4;
            Q4=makeQuery(id+"F9.boolean.opBoolean","COPY",EDGE,{"derivedFrom":makeQuery(id+"F9.opExtrude","SWEPT_EDGE",EDGE,{"disambiguationData":[OSD([sQuery(id+"F8.wireOp",EDGE,"E13.0"),sQuery(id+"F8.wireOp",EDGE,"E14")])]})});
            var Q5;
            Q5=makeQuery(id+"F9.boolean.opBoolean","COPY",EDGE,{"derivedFrom":makeQuery(id+"F9.opExtrude","CAP_EDGE",EDGE,{"disambiguationData":[OSD([sQuery(id+"F8.wireOp",EDGE,"E13.0")])],"isStart":false})});
            var Q6;
            Q6=makeQuery(id+"F9.boolean.opBoolean","COPY",EDGE,{"derivedFrom":makeQuery(id+"F9.opExtrude","SWEPT_EDGE",EDGE,{"disambiguationData":[OSD([sQuery(id+"F8.wireOp",EDGE,"E13.0"),sQuery(id+"F8.wireOp",EDGE,"E15")])]})});
            chamfer(context, id + "F12", {"entities" : qUnion([Q0, Q1, Q2, Q3, Q4, Q5, Q6]), "width" : .5 * mm, "tangentPropagation" : true});
        }
        {
            var Q0;
            Q0=qCreatedBy(makeId("Right.planeOp"),FACE);
            var sketch = newSketch(context, id + "F13", { "sketchPlane" : qUnion([Q0])});
            skLineSegment(sketch, "E21.0", {"start": v(2.98, 27.94) * mm, "end": v(-4.37, 27.94) * mm});
            skLineSegment(sketch, "E22", {"start": v(-3.87, 27.94) * mm, "end": v(-3.87, 19.94) * mm});
            skLineSegment(sketch, "E23", {"start": v(-3.87, 19.94) * mm, "end": v(-3.87, -10.24) * mm});
            skLineSegment(sketch, "E24", {"start": v(-3.87, -10.24) * mm, "end": v(-3.87, -18.24) * mm});
            skArc(sketch, "E25", {"start": v(-3.87, 19.94) * mm, "mid": v(-4.37, 4.85) * mm, "end": v(-3.87, -10.24) * mm});
            skPoint(sketch, "E26", {"position": v(-0.7, 27.94) * mm});
            skLineSegment(sketch, "E27", {"start": v(-0.7, 27.94) * mm, "end": v(-0.7, 6.76) * mm, "construction": true});
            skSolve(sketch);
        }
        {
            var Q0;
            Q0=makeQuery(id+"F13.imprint","IMPRINT",FACE,{"disambiguationData":[TD([[makeQuery(id+"F13.imprint","IMPRINT",EDGE,{"derivedFrom":sQuery(id+"F13.wireOp",EDGE,"E23")}),-1.0]])]});
            var Q1;
            Q1=sQuery(id+"F13.wireOp",EDGE,"E27");
            revolve(context, id + "F14", {"operationType" : NewBodyOperationType.REMOVE, "entities" : qUnion([Q0]), "axis" : qUnion([Q1]), "revolveType" : RevolveType.FULL, "oppositeDirection" : true});
        }
        {
            var Q0;
            Q0=makeQuery(id+"F5.opExtrude","CAP_FACE",FACE,{"disambiguationData":[OSD([sQuery(id+"F0.wireOp",EDGE,"E10"),sQuery(id+"F4.wireOp",EDGE,"E12")])],"isStart":false});
            var sketch = newSketch(context, id + "F15", { "sketchPlane" : qUnion([Q0])});
            skCircle(sketch, "E28", {"center": v(0, 0.7) * mm, "radius": 3.95 * mm});
            skSolve(sketch);
        }
        {
            var Q0;
            Q0=makeQuery(id+"F15.imprint","IMPRINT",FACE,{"disambiguationData":[TD([[makeQuery(id+"F15.imprint","IMPRINT",EDGE,{"derivedFrom":makeQuery(id+"F5.opExtrude","CAP_EDGE",EDGE,{"disambiguationData":[OSD([sQuery(id+"F0.wireOp",EDGE,"E10")])],"isStart":false})}),-1.0]])]});
            extrude(context, id + "F16", {"entities" : qUnion([Q0]), "operationType" : NewBodyOperationType.ADD, "oppositeDirection" : true, "depth" : 6.35 * mm, "offsetDistance" : 25.4 * mm});
        }
        {
            var Q0;
            Q0=makeQuery(id+"F15.imprint","IMPRINT",FACE,{"disambiguationData":[TD([[makeQuery(id+"F15.imprint","IMPRINT",EDGE,{"derivedFrom":sQuery(id+"F15.wireOp",EDGE,"E28")}),1.0]])]});
            var Q1;
            Q1=makeQuery(id+"F15.imprint","IMPRINT",FACE,{"disambiguationData":[TD([[makeQuery(id+"F15.imprint","IMPRINT",EDGE,{"derivedFrom":makeQuery(id+"F5.opExtrude","CAP_EDGE",EDGE,{"disambiguationData":[OSD([sQuery(id+"F0.wireOp",EDGE,"E10")])],"isStart":false})}),-1.0]])]});
            extrude(context, id + "F17", {"entities" : qUnion([Q0, Q1]), "operationType" : NewBodyOperationType.ADD, "depth" : 12.7 * mm, "offsetDistance" : 25.4 * mm});
        }
        {
            var Q0;
            Q0=makeQuery(id+"F17.opExtrude","CAP_EDGE",EDGE,{"disambiguationData":[OSD([sQuery(id+"F15.wireOp",EDGE,"E28")])],"isStart":true});
            var Q1;
            Q1=makeQuery(id+"F17.opExtrude","CAP_EDGE",EDGE,{"disambiguationData":[OSD([sQuery(id+"F15.wireOp",EDGE,"E28")])],"isStart":false});
            chamfer(context, id + "F18", {"entities" : qUnion([Q0, Q1]), "width" : 1.27 * mm, "tangentPropagation" : true});
        }
    });
